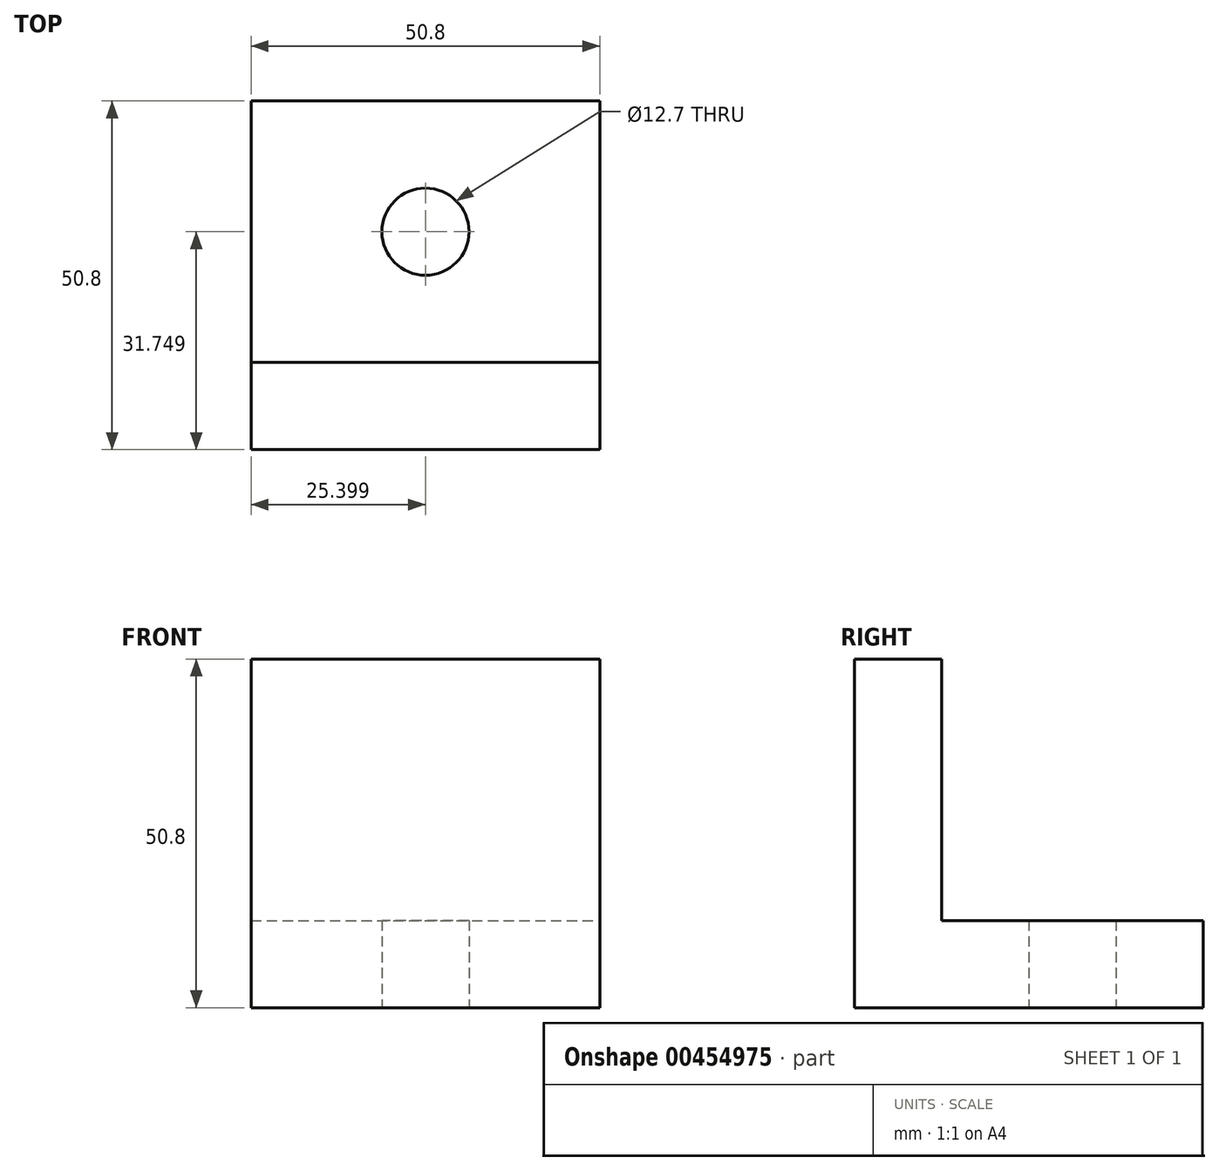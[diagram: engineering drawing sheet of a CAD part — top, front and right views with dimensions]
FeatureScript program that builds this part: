
annotation { "Feature Type Name" : "Feature", "Feature Type Description" : "" }
export const myFeature = defineFeature(function(context is Context, id is Id, definition is map)
    precondition{}
    {
        {
            var Q0;
            Q0=qCreatedBy(makeId("Top.planeOp"),FACE);
            var sketch = newSketch(context, id + "F0", { "sketchPlane" : qUnion([Q0])});
            skLineSegment(sketch, "E0.bottom", {"start": v(-21.7, 33.57) * mm, "end": v(29.1, 33.57) * mm});
            skLineSegment(sketch, "E0.top", {"start": v(-21.7, -17.23) * mm, "end": v(29.1, -17.23) * mm});
            skLineSegment(sketch, "E0.left", {"start": v(-21.7, 33.57) * mm, "end": v(-21.7, -17.23) * mm});
            skLineSegment(sketch, "E0.right", {"start": v(29.1, 33.57) * mm, "end": v(29.1, -17.23) * mm});
            skLineSegment(sketch, "E1.top", {"start": v(-21.7, -4.53) * mm, "end": v(29.1, -4.53) * mm});
            skLineSegment(sketch, "E1.left", {"start": v(-21.7, -17.23) * mm, "end": v(-21.7, -4.53) * mm});
            skLineSegment(sketch, "E1.right", {"start": v(29.1, -17.23) * mm, "end": v(29.1, -4.53) * mm});
            skCircle(sketch, "E2", {"center": v(3.7, 14.52) * mm, "radius": 6.35 * mm});
            skSolve(sketch);
        }
        {
            var Q0;
            Q0=makeQuery(id+"F0.imprint","IMPRINT",FACE,{"disambiguationData":[TD([[makeQuery(id+"F0.imprint","IMPRINT",EDGE,{"derivedFrom":sQuery(id+"F0.wireOp",EDGE,"E0.bottom")}),-1.0]])]});
            extrude(context, id + "F1", {"entities" : qUnion([Q0]), "depth" : 12.7 * mm});
        }
        {
            var Q0;
            Q0=makeQuery(id+"F0.imprint","IMPRINT",FACE,{"disambiguationData":[TD([[makeQuery(id+"F0.imprint","IMPRINT",EDGE,{"derivedFrom":sQuery(id+"F0.wireOp",EDGE,"E0.top")}),1.0]])]});
            extrude(context, id + "F2", {"entities" : qUnion([Q0]), "operationType" : NewBodyOperationType.ADD, "depth" : 50.8 * mm});
        }
    });
